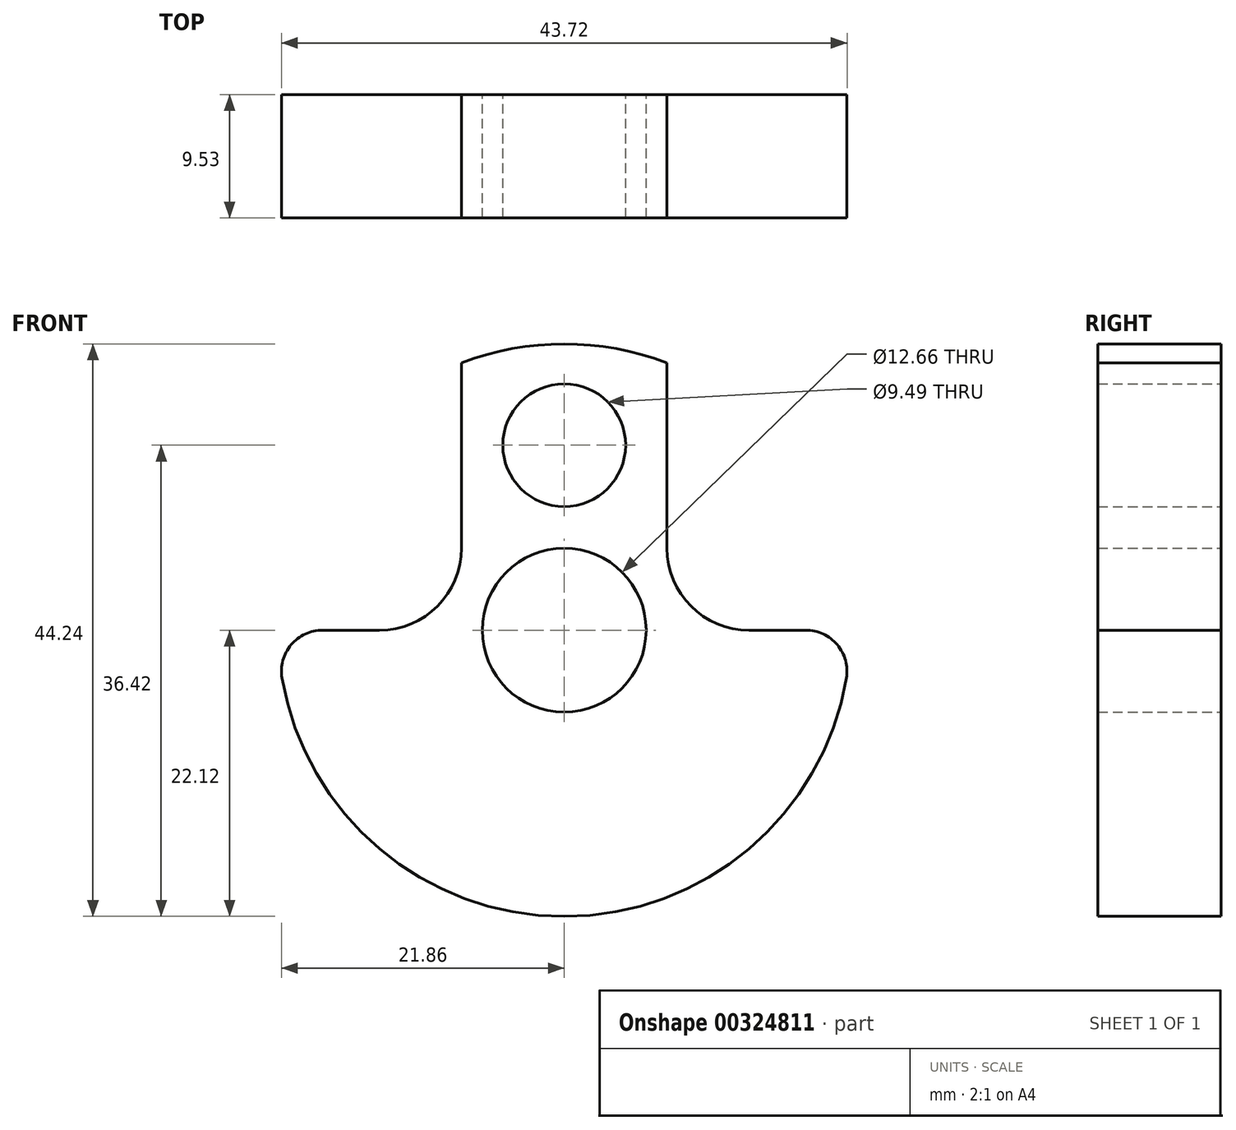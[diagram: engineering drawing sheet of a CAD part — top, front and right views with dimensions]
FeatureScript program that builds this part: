
annotation { "Feature Type Name" : "Feature", "Feature Type Description" : "" }
export const myFeature = defineFeature(function(context is Context, id is Id, definition is map)
    precondition{}
    {
        {
            var Q0;
            Q0=qCreatedBy(makeId("Front.planeOp"),FACE);
            var sketch = newSketch(context, id + "F0", { "sketchPlane" : qUnion([Q0])});
            skArc(sketch, "E0", {"start": v(-22.12, 0) * mm, "mid": v(0, -22.12) * mm, "end": v(22.12, 0) * mm});
            skCircle(sketch, "E1", {"center": v(0, 0) * mm, "radius": 6.33 * mm});
            skLineSegment(sketch, "E2", {"start": v(-7.94, 0) * mm, "end": v(-7.94, 20.65) * mm});
            skLineSegment(sketch, "E3.MirrorCS", {"start": v(7.94, 0) * mm, "end": v(7.94, 20.65) * mm});
            skLineSegment(sketch, "E4", {"start": v(-7.94, 0) * mm, "end": v(-22.12, 0) * mm});
            skLineSegment(sketch, "E5", {"start": v(7.94, 0) * mm, "end": v(22.12, 0) * mm});
            skCircle(sketch, "E6", {"center": v(0, 14.3) * mm, "radius": 4.74 * mm});
            skArc(sketch, "E7.trimOffspring", {"start": v(7.94, 20.65) * mm, "mid": v(0, 22.12) * mm, "end": v(-7.94, 20.65) * mm});
            skSolve(sketch);
        }
        {
            var Q0;
            Q0=makeQuery(id+"F0.imprint","IMPRINT",FACE,{"disambiguationData":[TD([[makeQuery(id+"F0.imprint","IMPRINT",EDGE,{"derivedFrom":sQuery(id+"F0.wireOp",EDGE,"E0")}),1.0]])]});
            extrude(context, id + "F1", {"entities" : qUnion([Q0]), "depth" : 9.52 * mm, "offsetDistance" : 25.4 * mm});
        }
        {
            var Q0;
            Q0=makeQuery(id+"F1.opExtrude","SWEPT_EDGE",EDGE,{"disambiguationData":[OSD([sQuery(id+"F0.wireOp",EDGE,"E2"),sQuery(id+"F0.wireOp",EDGE,"E4")])]});
            var Q1;
            Q1=makeQuery(id+"F1.opExtrude","SWEPT_EDGE",EDGE,{"disambiguationData":[OSD([sQuery(id+"F0.wireOp",EDGE,"E3.MirrorCS"),sQuery(id+"F0.wireOp",EDGE,"E5")])]});
            fillet(context, id + "F2", {"entities" : qUnion([Q0, Q1]), "radius" : 6.35 * mm, "tangentPropagation" : true, "allowEdgeOverflow" : false});
        }
        {
            var Q0;
            Q0=makeQuery(id+"F1.opExtrude","SWEPT_EDGE",EDGE,{"disambiguationData":[OSD([sQuery(id+"F0.wireOp",EDGE,"E0"),sQuery(id+"F0.wireOp",EDGE,"E4")])]});
            var Q1;
            Q1=makeQuery(id+"F1.opExtrude","SWEPT_EDGE",EDGE,{"disambiguationData":[OSD([sQuery(id+"F0.wireOp",EDGE,"E0"),sQuery(id+"F0.wireOp",EDGE,"E5")])]});
            fillet(context, id + "F3", {"entities" : qUnion([Q0, Q1]), "radius" : 3.17 * mm, "tangentPropagation" : true, "allowEdgeOverflow" : false});
        }
    });
